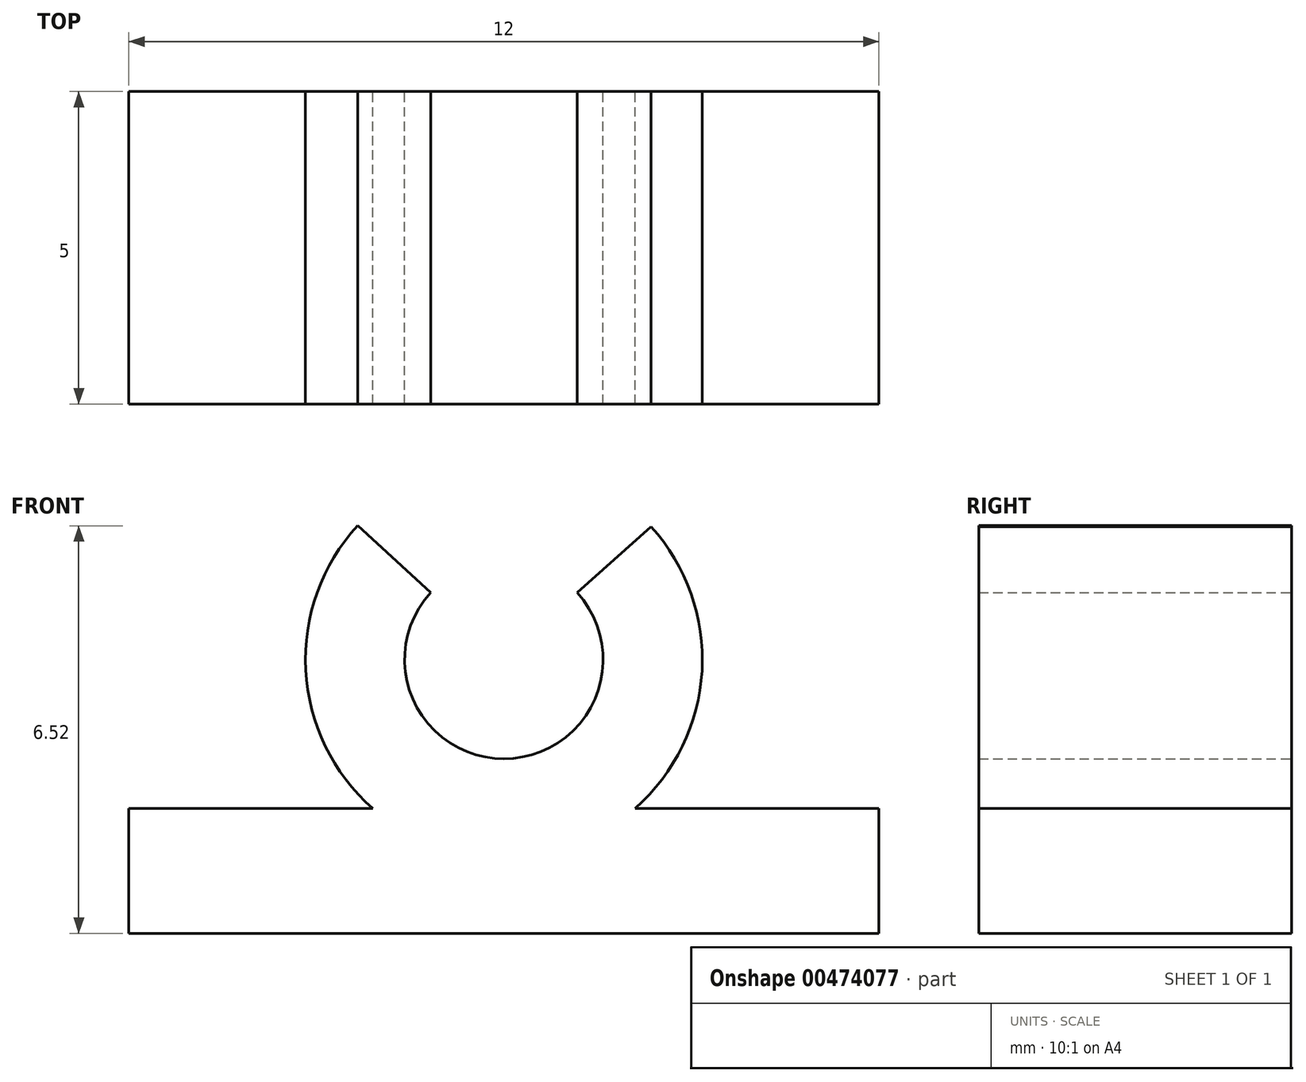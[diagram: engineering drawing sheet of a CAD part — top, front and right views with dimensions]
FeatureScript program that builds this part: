
annotation { "Feature Type Name" : "Feature", "Feature Type Description" : "" }
export const myFeature = defineFeature(function(context is Context, id is Id, definition is map)
    precondition{}
    {
        {
            var Q0;
            Q0=qCreatedBy(makeId("Front.planeOp"),FACE);
            var sketch = newSketch(context, id + "F0", { "sketchPlane" : qUnion([Q0])});
            skArc(sketch, "E0", {"start": v(-1.17, 1.07) * mm, "mid": v(0, -1.59) * mm, "end": v(1.17, 1.07) * mm});
            skArc(sketch, "E1", {"start": v(-2.34, 2.14) * mm, "mid": v(-0.01, -3.17) * mm, "end": v(2.36, 2.13) * mm});
            skLineSegment(sketch, "E2", {"start": v(-2.34, 2.14) * mm, "end": v(-1.17, 1.07) * mm});
            skLineSegment(sketch, "E3", {"start": v(2.36, 2.13) * mm, "end": v(1.17, 1.07) * mm});
            skLineSegment(sketch, "E4.bottom", {"start": v(-6, -2.38) * mm, "end": v(6, -2.38) * mm});
            skLineSegment(sketch, "E4.top", {"start": v(-6, -4.38) * mm, "end": v(6, -4.38) * mm});
            skLineSegment(sketch, "E4.left", {"start": v(6, -2.38) * mm, "end": v(6, -4.38) * mm});
            skLineSegment(sketch, "E4.right", {"start": v(-6, -2.38) * mm, "end": v(-6, -4.38) * mm});
            skLineSegment(sketch, "E5", {"start": v(0, -1.59) * mm, "end": v(0, -3.18) * mm});
            skLineSegment(sketch, "E6", {"start": v(0, -1.59) * mm, "end": v(0, -2.38) * mm});
            skSolve(sketch);
        }
        {
            var Q0;
            Q0 = qSketchRegion(id + "F0", true);
            extrude(context, id + "F1", {"entities" : qUnion([Q0]), "depth" : 5 * mm});
        }
    });
